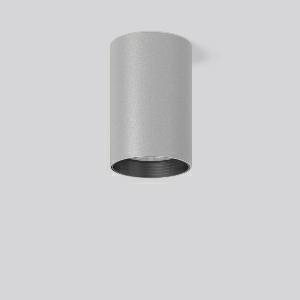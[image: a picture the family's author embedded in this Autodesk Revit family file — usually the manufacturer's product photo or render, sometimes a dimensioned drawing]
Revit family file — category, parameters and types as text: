
# Revit family: heledon_maxi_a_931228_004_2_76_41f1
name_source: partatom
category: Lighting Fixtures
units: mm (PartAtom-declared; Revit-internal decimal feet)

## family parameters
Cut with Voids When Loaded = No
Host = Face
Light Source = No
Part Type = Normal
Room Calculation Point = No
Round Connector Dimension = Use Diameter
Shared = No

## types (1)
- HELEDON maxi A (1 x LED Modul 927, 3350 lm, 2700)
    Apparent Load = 35 VA
    Approval mark = CE
    CIE Flux Codes = 96 100 100 100 100
    Color Rendering = 92
    Color Temperature = 2700
    Default Elevation = 1800 mm
    Description = Series: HELEDON maxi
Cylindrical surface-mounted downlight. Housing: die-cast aluminium, powder-coated. Internal ceiling frame polycarbonate with bayonet mounting. Black plastic ring and recessed LED to prevent glare from the side. Optical assembly with lens made of plastic (polycarbonate) for the best homogeneous light distribution - can be changed without tools. Best colour rendering index Ra>90. Suitable for Ceiling mounting. Easy installation with a separate ceiling frame with bayonet mounting and plug connection. Driver integrated. Connected via plug-in connector. High quality converter without flickering and stroboscopic effect. The following accessories can be mounted without use of tools: interchangeable lenses, decorative glasses, honeycomb louvre, clear and frosted diffusers, white interchangeable plastic ring. 
Colour: silver
Diameter: 123 mm
Height: 183 mm
Lamp: LED
Socket: without socket
Colour temperature: 2700K
Colour rendering index (CRI): 92
System power: 35 W
Rated luminous flux: 3350 lm
Luminous efficiency: 96 lm/W
Control gear: Converter, dimmable, DALI
Protection class: I
Type of protection: IP 20
    Height = 183 mm
    Lamp = 1 x LED Modul 927
    Lamp Light Flux = 3350 lm
    Lamp count = 1
    Length = 123 mm
    Lifetime = 50000 h
    Luminous efficacy = 96 lm/W
    Manufacturer = RZB
    ModVariant = No
    Model = 931228.004.2.76
    Mounting Place = Ceiling
    Mounting Type = Surface mounted
    Number of Poles = 1
    OnlyDefault = Yes
    Power Factor = 1
    Product Name = HELEDON maxi A
    Product group = Surface mounted downlights
    ProductGroupID = 302
    Protection Class = Protection class I
    Protection Degree = IP 20
    RLX_Detail_Level = 1
    RLX_Emergency_Light_Flux = 0 lm
    RLX_Emergency_Type = 0
    RLX_Emergency_Type_DB = No
    RlxData = <blob elided: 99477 chars, md5=52ce6994>
    Socket = socket
    Standby Power = 0 W
    System Light Flux = 3350 lm
    System Power = 35 W
    Type Comments = Product without accessories
    Type Image = 931193.004.jpg
    URL = http://relux.com
    VarID = ---
    Voltage = 230 V
    Voltage Range = 220-240 V
    Weight = 0.00 kg
    Width = 0 mm  [stored 0 ft]

note: [stored X ft] marks values corroborated as IEEE doubles in the binary element streams (Revit-internal decimal feet)

## geometry (parser evidence)
native form markers: Blend x4, Sweep x11
no freeform markers — native parametric forms only
